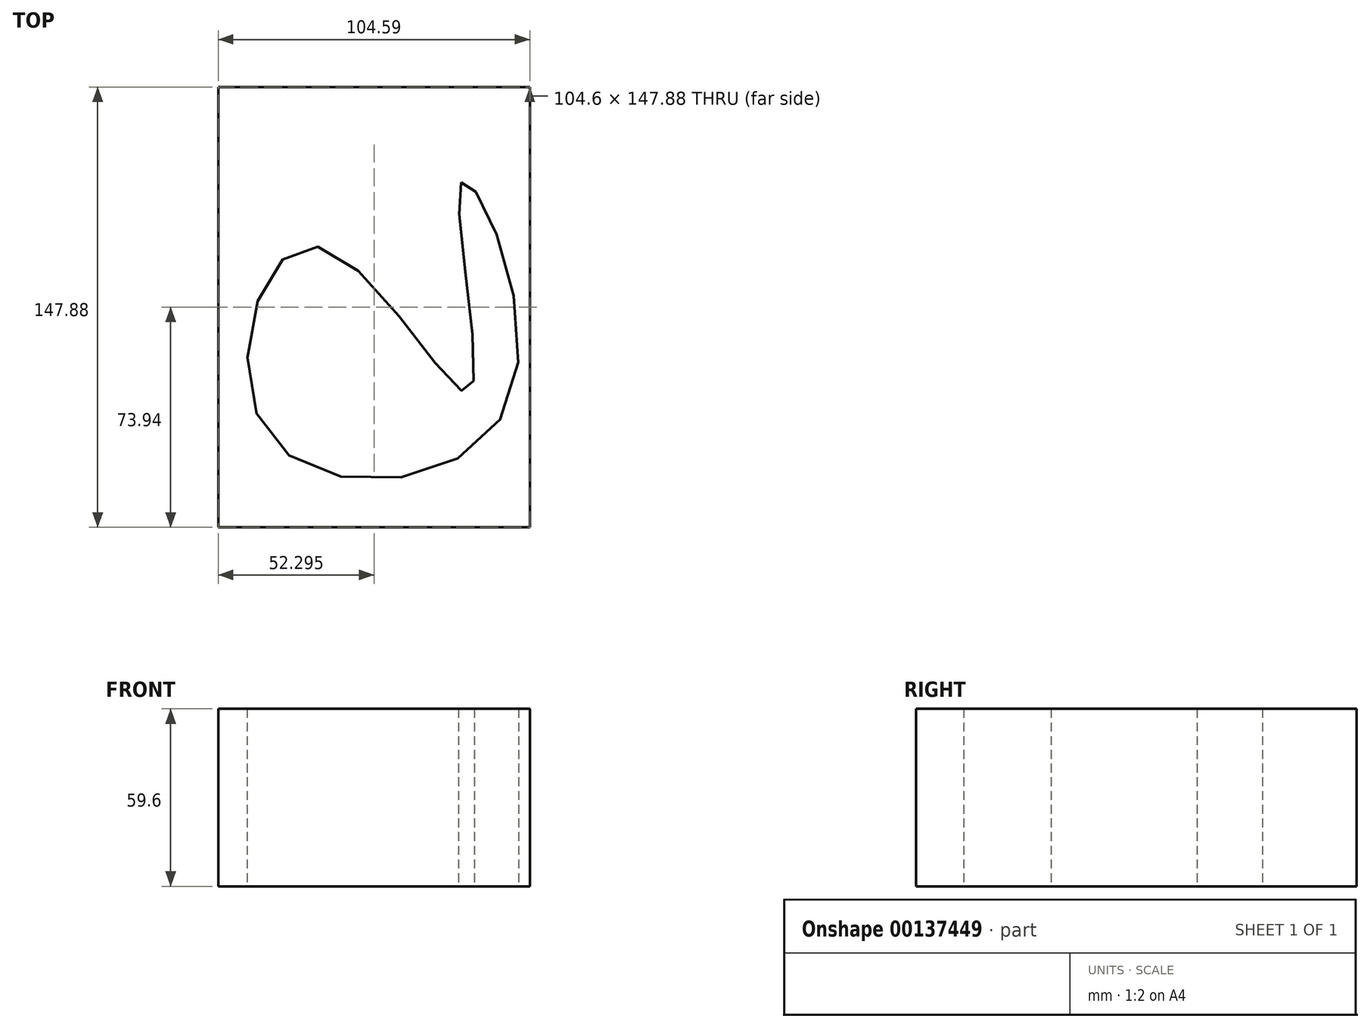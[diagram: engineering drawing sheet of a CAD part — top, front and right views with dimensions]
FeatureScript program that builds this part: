
annotation { "Feature Type Name" : "Feature", "Feature Type Description" : "" }
export const myFeature = defineFeature(function(context is Context, id is Id, definition is map)
    precondition{}
    {
        {
            var Q0;
            Q0=qCreatedBy(makeId("Top.planeOp"),FACE);
            var sketch = newSketch(context, id + "F0", { "sketchPlane" : qUnion([Q0])});
            skLineSegment(sketch, "E0.bottom", {"start": v(-54.3, 74.93) * mm, "end": v(50.3, 74.93) * mm});
            skLineSegment(sketch, "E0.top", {"start": v(-54.3, -72.95) * mm, "end": v(50.3, -72.95) * mm});
            skLineSegment(sketch, "E0.left", {"start": v(-54.3, 74.93) * mm, "end": v(-54.3, -72.95) * mm});
            skLineSegment(sketch, "E0.right", {"start": v(50.3, 74.93) * mm, "end": v(50.3, -72.95) * mm});
            skSolve(sketch);
        }
        {
            var Q0;
            Q0=makeQuery(id+"F0.imprint","IMPRINT",FACE,{"disambiguationData":[TD([[makeQuery(id+"F0.imprint","IMPRINT",EDGE,{"derivedFrom":sQuery(id+"F0.wireOp",EDGE,"E0.bottom")}),-1.0]])]});
            extrude(context, id + "F1", {"entities" : qUnion([Q0]), "depth" : 59.6 * mm});
        }
        {
            var Q0;
            Q0=makeQuery(id+"F1.opExtrude","SWEPT_FACE",FACE,{"disambiguationData":[OSD([sQuery(id+"F0.wireOp",EDGE,"E0.top")])]});
            extrude(context, id + "F2", {"entities" : qUnion([Q0]), "operationType" : NewBodyOperationType.ADD, "oppositeDirection" : true, "depth" : 67.75 * mm});
        }
        {
            var Q0;
            Q0=makeQuery(id+"F1.opExtrude","CAP_FACE",FACE,{"disambiguationData":[OSD([sQuery(id+"F0.wireOp",EDGE,"E0.bottom"),sQuery(id+"F0.wireOp",EDGE,"E0.top"),sQuery(id+"F0.wireOp",EDGE,"E0.left"),sQuery(id+"F0.wireOp",EDGE,"E0.right")])],"isStart":false});
            var sketch = newSketch(context, id + "F3", { "sketchPlane" : qUnion([Q0])});
            skFitSpline(sketch, "E1", {"points": [v(27.27, 42.88) * mm, v(29.98, -27.37) * mm, v(-21.83, 21.36) * mm, v(-37.96, -41.4) * mm, v(43, -31.9) * mm, v(27.27, 42.88) * mm]});
            skSolve(sketch);
        }
        {
            var Q0;
            Q0=makeQuery(id+"F3.imprint","IMPRINT",FACE,{"disambiguationData":[TD([[makeQuery(id+"F3.imprint","IMPRINT",EDGE,{"derivedFrom":sQuery(id+"F3.wireOp",EDGE,"E1")}),1.0]])]});
            extrude(context, id + "F4", {"entities" : qUnion([Q0]), "operationType" : NewBodyOperationType.REMOVE, "oppositeDirection" : true, "depth" : 109.8 * mm});
        }
    });
